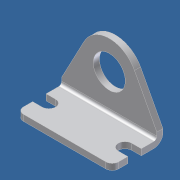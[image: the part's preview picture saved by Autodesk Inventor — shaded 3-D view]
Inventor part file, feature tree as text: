
AUTODESK INVENTOR PART (.ipt)
format: ipt  version: unknown  size: 245,248 bytes
history: native  units: in
note: dims shown in document units (in); Inventor stores cm internally (conversion verified against a paired STEP export)
features: other x126, extrude x7, sketch x7
ambient origin geometry x8: Origin, YZ Plane, XZ Plane, XY Plane, X Axis, Y Axis, Z Axis, Center Point
feature tree (140):
  extrude  "Extrusion1"  Depth=0.18in TaperAngle=0.0deg
  extrude  "Extrusion2"  Depth=0.18in TaperAngle=0.0deg
  extrude  "Extrusion3"  Depth=0.18in TaperAngle=0.0deg
  extrude  "Extrusion4"  [1 undecoded]
  extrude  "Extrusion5"  [1 undecoded]
  extrude  "Extrusion6"  [1 undecoded]
  extrude  "Extrusion7"  [1 undecoded]
  other  "h1_XY"
  other  "h1_YZ"
  other  "h1_ZX"
  other  "h1_X"
  other  "h1_Y"
  other  "h1_Z"
  other  "h1_Center"
  other  "d1_XY"
  other  "d1_YZ"
  other  "d1_ZX"
  other  "d1_X"
  other  "d1_Y"
  other  "d1_Z"
  other  "d1_Center"
  other  "h2_XY"
  other  "h2_YZ"
  other  "h2_ZX"
  other  "h2_X"
  other  "h2_Y"
  other  "h2_Z"
  other  "h2_Center"
  other  "d2_XY"
  other  "d2_YZ"
  other  "d2_ZX"
  other  "d2_X"
  other  "d2_Y"
  other  "d2_Z"
  other  "d2_Center"
  other  "h3_XY"
  other  "h3_YZ"
  other  "h3_ZX"
  other  "h3_X"
  other  "h3_Y"
  other  "h3_Z"
  other  "h3_Center"
  other  "h4_XY"
  other  "h4_YZ"
  other  "h4_ZX"
  other  "h4_X"
  other  "h4_Y"
  other  "h4_Z"
  other  "h4_Center"
  other  "h5_XY"
  other  "h5_YZ"
  other  "h5_ZX"
  other  "h5_X"
  other  "h5_Y"
  other  "h5_Z"
  other  "h5_Center"
  other  "h6_XY"
  other  "h6_YZ"
  other  "h6_ZX"
  other  "h6_X"
  other  "h6_Y"
  other  "h6_Z"
  other  "h6_Center"
  other  "l1_XY"
  other  "l1_YZ"
  other  "l1_ZX"
  other  "l1_X"
  other  "l1_Y"
  other  "l1_Z"
  other  "l1_Center"
  other  "l2_XY"
  other  "l2_YZ"
  other  "l2_ZX"
  other  "l2_X"
  other  "l2_Y"
  other  "l2_Z"
  other  "l2_Center"
  other  "l3_XY"
  other  "l3_YZ"
  other  "l3_ZX"
  other  "l3_X"
  other  "l3_Y"
  other  "l3_Z"
  other  "l3_Center"
  other  "l4_XY"
  other  "l4_YZ"
  other  "l4_ZX"
  other  "l4_X"
  other  "l4_Y"
  other  "l4_Z"
  other  "l4_Center"
  other  "l5_XY"
  other  "l5_YZ"
  other  "l5_ZX"
  other  "l5_X"
  other  "l5_Y"
  other  "l5_Z"
  other  "l5_Center"
  other  "l6_XY"
  other  "l6_YZ"
  other  "l6_ZX"
  other  "l6_X"
  other  "l6_Y"
  other  "l6_Z"
  other  "l6_Center"
  other  "l7_XY"
  other  "l7_YZ"
  other  "l7_ZX"
  other  "l7_X"
  other  "l7_Y"
  other  "l7_Z"
  other  "l7_Center"
  other  "l8_XY"
  other  "l8_YZ"
  other  "l8_ZX"
  other  "l8_X"
  other  "l8_Y"
  other  "l8_Z"
  other  "l8_Center"
  other  "mounting_bracket_XY"
  other  "mounting_bracket_YZ"
  other  "mounting_bracket_ZX"
  other  "mounting_bracket_X"
  other  "mounting_bracket_Y"
  other  "mounting_bracket_Z"
  other  "mounting_bracket_Center"
  other  "mounting_bracket_1_XY"
  other  "mounting_bracket_1_YZ"
  other  "mounting_bracket_1_ZX"
  other  "mounting_bracket_1_X"
  other  "mounting_bracket_1_Y"
  other  "mounting_bracket_1_Z"
  other  "mounting_bracket_1_Center"
  sketch  "Sketch_1"  dims[d0=1.875in d1=0.0in d2=0.18in d3=0.0in]
  sketch  "Sketch_2"  dims[d4=0.18in d5=0.0in d6=0.18in d7=0.0in]
  sketch  "Sketch_3"  dims[d8=0.18in d9=0.0in d10=0.18in d11=0.0in]
  sketch  "Sketch_6"  dims[d12=0.18in d13=0.0in]
  sketch  "Sketch_7"
  sketch  "Sketch_8"
  sketch  "Sketch_9"
note: 4 required parameter values undecoded (feature->parameter linkage not recoverable at this tier; creation-order binding heuristic only, values carry confidence <= 0.55)
